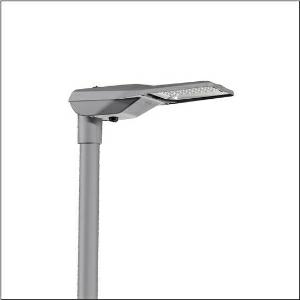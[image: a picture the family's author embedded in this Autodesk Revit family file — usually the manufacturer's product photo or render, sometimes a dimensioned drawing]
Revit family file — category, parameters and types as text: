
# Revit family: streetlight_sl_21_mini___st0_8a_5xe2c43t08hb_23df
name_source: partatom
category: Lighting Fixtures
units: mm (PartAtom-declared; Revit-internal decimal feet)

## family parameters
Cut with Voids When Loaded = No
Host = Face
Light Source = No
Part Type = Normal
Room Calculation Point = No
Round Connector Dimension = Use Diameter
Shared = No

## types (1)
- --- (1 x LED, 9430 lm, 66 W, 4000K)
    Apparent Load = 66 VA
    CIE Flux Codes = 38 75 97 100 100
    Color Rendering = 70
    Color Temperature = 4000K
    Default Elevation = 1800 mm
    Description = Streetlight SL 21 mini, mast luminaire, primary light control with lens, of PMMA, primary optical cover: cover, of toughened safety glass, transparent, light distribution: ST0.8a, light emission: direct distribution, primary light characteristic: asymmetric, installation type: side-entry, post-top, LED, High Power LED, rated luminous flux: 9.430lm, luminous efficacy: 143lm/W, light colour: 740, colour temperature: 4000K, control gear: D4i, control: overheat protection, constant luminous flux control, time-dependent luminous flux control, flexible luminous flux parameterisation, pre-setting: logarithmic dimming characteristic, mains connection: 220..240V, AC, 50/60Hz, start of lifetime: 66W, end of service life: 69W, reduction: 30W, luminaire housing, of diecast aluminium, powder-coated, SITECO metallic grey (DB 702S), corrosivity category C5 high according to DIN EN ISO 12944, please order mast flange separately, inclination adjustable: 0°, 5°, 10°, 15°, sealing non-destructively replaceable, multi-level sealing system, length: 628mm, width: 235mm, height: 110mm, mast flange for spigot size: 42mm (side-entry): 5XC10008XM4, 60/48mm (side-entry/post-top): 5XC10108XM2, 76/60mm (side-entry/post-top): 5XC10108XM1, mounting height: 4..8m, Smart Interface below and above, protection rating (complete): IP66, insulation class (complete): insulation class II (safety insulation), certification: CE, ENEC, ENEC+, VDE, impact resistance: IK10, permissible operating ambient temperature for outdoor applications: -40..+50°C, standard-compliant lighting for roads and squares, packaging unit: 1 piece

Light Distribution: ST0.8a
    Height = 110 mm
    Lamp = 1 x LED
    Lamp Light Flux = 9430 lm
    Lamp Power = 66 W
    Lamp count = 1
    Length = 625 mm
    Luminous efficacy = 143 lm/W
    Manufacturer = Siteco
    ModVariant = No
    Model = 5XE2C43T08HB
    Number of Poles = 1
    OnlyDefault = Yes
    Power Factor = 1
    Product Name = Streetlight SL 21 mini | ST0.8a
    Product group = mast luminaire | pylon top
    ProductGroupID = 6100
    Protection Class = Protection class II
    Protection Degree = IP 66
    RLX_Detail_Level = 1
    RLX_Emergency_Light_Flux = 0 lm
    RLX_Emergency_Type = 0
    RLX_Emergency_Type_DB = No
    RlxData = <blob elided: 26329 chars, md5=562835df>
    Socket = socket
    Standby Power = 0 W
    System Light Flux = 9430 lm
    System Power = 66 W
    Type Comments = factory setting: luminous flux: 100 % | dim-lin: 254 | 670 mA
    Type Image = l_1003514.jpg
    URL = http://relux.com
    VarID = @adj_182735
    Voltage = 0 V
    Weight = 0.00 kg
    Width = 234 mm

## geometry (parser evidence)
native form markers: Blend x4, Sweep x12
no freeform markers — native parametric forms only
